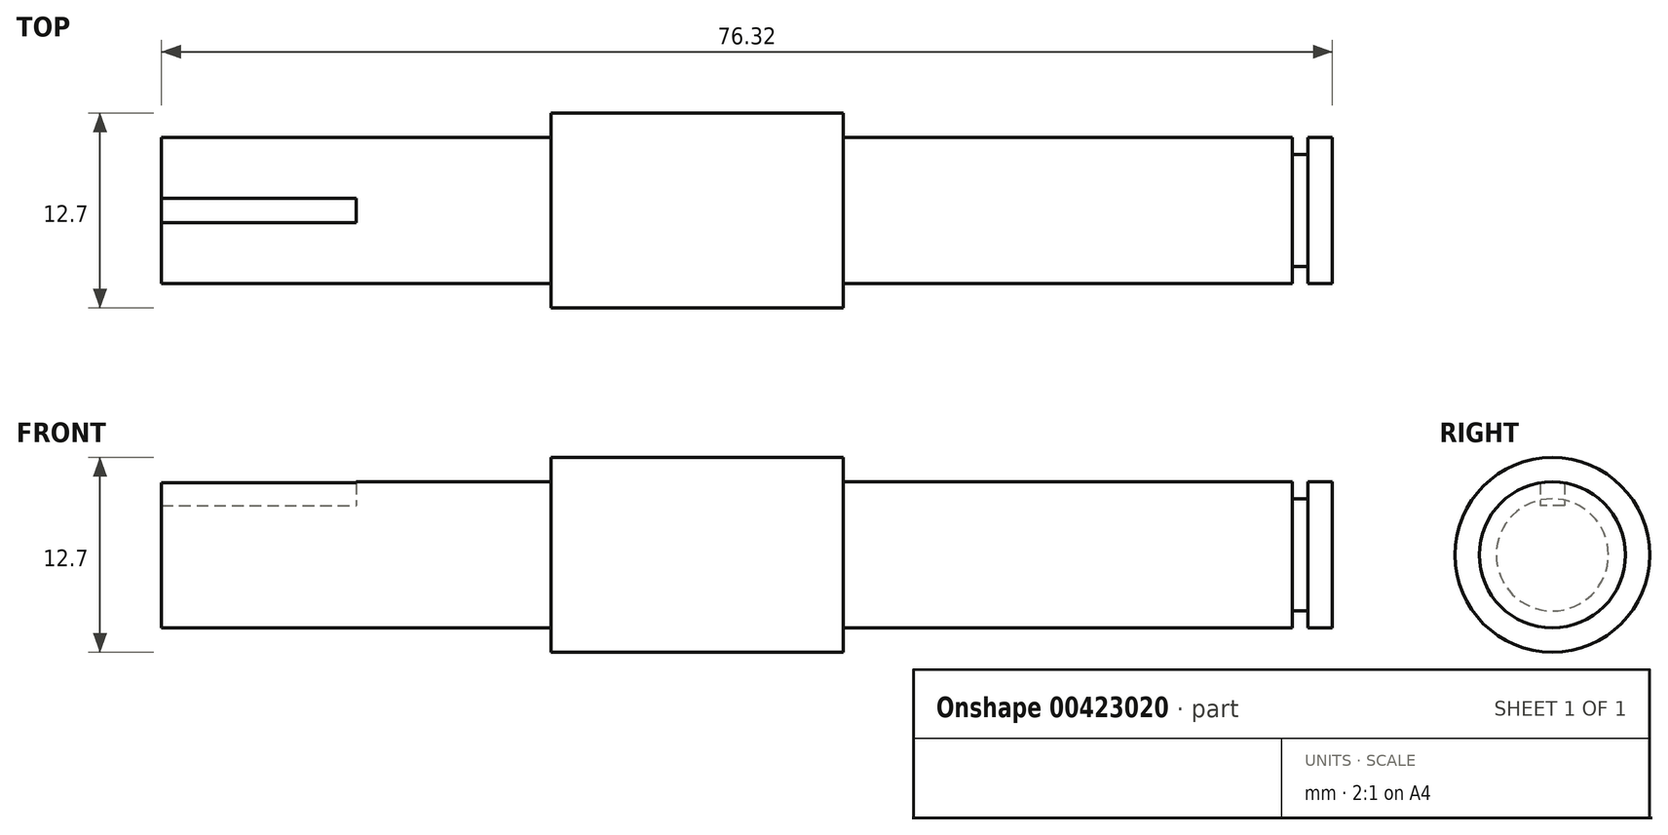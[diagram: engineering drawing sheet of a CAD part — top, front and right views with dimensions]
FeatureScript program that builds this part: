
annotation { "Feature Type Name" : "Feature", "Feature Type Description" : "" }
export const myFeature = defineFeature(function(context is Context, id is Id, definition is map)
    precondition{}
    {
        {
            var Q0;
            Q0=qCreatedBy(makeId("Front.planeOp"),FACE);
            var sketch = newSketch(context, id + "F0", { "sketchPlane" : qUnion([Q0])});
            skLineSegment(sketch, "E0.bottom", {"start": v(3.17, 2.38) * mm, "end": v(-3.18, 2.38) * mm});
            skLineSegment(sketch, "E0.top", {"start": v(3.18, -2.38) * mm, "end": v(-3.17, -2.38) * mm});
            skLineSegment(sketch, "E0.left", {"start": v(3.17, 2.38) * mm, "end": v(3.18, -2.38) * mm});
            skLineSegment(sketch, "E0.right", {"start": v(-3.18, 2.38) * mm, "end": v(-3.17, -2.38) * mm});
            skPoint(sketch, "E0.middle", {"position": v(0, 0) * mm});
            skLineSegment(sketch, "E1.bottom", {"start": v(3.18, -2.38) * mm, "end": v(7.77, -2.38) * mm});
            skLineSegment(sketch, "E1.top", {"start": v(3.17, 2.38) * mm, "end": v(7.77, 2.38) * mm});
            skLineSegment(sketch, "E1.left", {"start": v(3.18, -2.38) * mm, "end": v(3.17, 2.38) * mm});
            skLineSegment(sketch, "E1.right", {"start": v(7.77, -2.38) * mm, "end": v(7.77, 2.38) * mm});
            skLineSegment(sketch, "E2.bottom", {"start": v(-3.17, -2.38) * mm, "end": v(-7.77, -2.38) * mm});
            skLineSegment(sketch, "E2.top", {"start": v(-3.18, 2.38) * mm, "end": v(-7.77, 2.38) * mm});
            skLineSegment(sketch, "E2.left", {"start": v(-3.17, -2.38) * mm, "end": v(-3.18, 2.38) * mm});
            skLineSegment(sketch, "E2.right", {"start": v(-7.77, -2.38) * mm, "end": v(-7.77, 2.38) * mm});
            skPoint(sketch, "E3.oppositeSnap0", {"position": v(0, -2.38) * mm});
            skLineSegment(sketch, "E3.bottom", {"start": v(7.77, 2.38) * mm, "end": v(14.12, 2.38) * mm});
            skLineSegment(sketch, "E3.top", {"start": v(7.77, -2.38) * mm, "end": v(14.12, -2.38) * mm});
            skLineSegment(sketch, "E3.left", {"start": v(7.77, 2.38) * mm, "end": v(7.77, -2.38) * mm});
            skLineSegment(sketch, "E3.right", {"start": v(14.12, 2.38) * mm, "end": v(14.12, -2.38) * mm});
            skLineSegment(sketch, "E4.bottom", {"start": v(-7.77, -2.38) * mm, "end": v(-14.12, -2.38) * mm});
            skLineSegment(sketch, "E4.top", {"start": v(-7.77, 2.38) * mm, "end": v(-14.12, 2.38) * mm});
            skLineSegment(sketch, "E4.right", {"start": v(-14.12, -2.38) * mm, "end": v(-14.12, 2.38) * mm});
            skLineSegment(sketch, "E5.bottom", {"start": v(-14.12, -2.38) * mm, "end": v(-15.14, -2.38) * mm});
            skLineSegment(sketch, "E5.top", {"start": v(-14.12, 2.38) * mm, "end": v(-15.14, 2.38) * mm});
            skLineSegment(sketch, "E5.right", {"start": v(-15.14, -2.38) * mm, "end": v(-15.14, 2.38) * mm});
            skLineSegment(sketch, "E6.bottom", {"start": v(-15.14, -2.38) * mm, "end": v(-34.19, -2.38) * mm});
            skLineSegment(sketch, "E6.top", {"start": v(-15.14, 3.97) * mm, "end": v(-34.19, 3.97) * mm});
            skLineSegment(sketch, "E6.left", {"start": v(-15.14, -2.38) * mm, "end": v(-15.14, 3.97) * mm});
            skLineSegment(sketch, "E6.right", {"start": v(-34.19, -0.8) * mm, "end": v(-34.19, 3.97) * mm});
            skLineSegment(sketch, "E7.bottom", {"start": v(14.12, -2.38) * mm, "end": v(15.14, -2.38) * mm});
            skLineSegment(sketch, "E7.top", {"start": v(14.12, 1.27) * mm, "end": v(15.14, 1.27) * mm});
            skLineSegment(sketch, "E7.left", {"start": v(14.12, -2.38) * mm, "end": v(14.12, 1.27) * mm});
            skLineSegment(sketch, "E7.right", {"start": v(15.14, -2.38) * mm, "end": v(15.14, 1.27) * mm});
            skLineSegment(sketch, "E8.bottom", {"start": v(15.14, -2.38) * mm, "end": v(16.73, -2.38) * mm});
            skLineSegment(sketch, "E8.top", {"start": v(15.14, 2.38) * mm, "end": v(16.73, 2.38) * mm});
            skLineSegment(sketch, "E8.left", {"start": v(15.14, -2.38) * mm, "end": v(15.14, 2.38) * mm});
            skLineSegment(sketch, "E8.right", {"start": v(16.73, -2.38) * mm, "end": v(16.73, 2.38) * mm});
            skLineSegment(sketch, "E9.bottom", {"start": v(-34.19, -2.38) * mm, "end": v(-59.59, -2.38) * mm});
            skLineSegment(sketch, "E9.top", {"start": v(-34.19, 2.38) * mm, "end": v(-59.59, 2.38) * mm});
            skLineSegment(sketch, "E9.left", {"start": v(-34.19, -2.38) * mm, "end": v(-34.19, 2.38) * mm});
            skLineSegment(sketch, "E9.right", {"start": v(-59.59, -2.38) * mm, "end": v(-59.59, 2.38) * mm});
            skSolve(sketch);
        }
        {
            var Q0;
            Q0=qSketchRegion(id+"F0",true);
            var Q1;
            Q1=sQuery(id+"F0.wireOp",EDGE,"E0.top");
            revolve(context, id + "F1", {"entities" : qUnion([Q0]), "axis" : qUnion([Q1]), "revolveType" : RevolveType.FULL});
        }
        {
            var Q0;
            Q0=qCreatedBy(makeId("Front.planeOp"),FACE);
            var sketch = newSketch(context, id + "F2", { "sketchPlane" : qUnion([Q0])});
            skLineSegment(sketch, "E10.bottom", {"start": v(-59.59, 2.42) * mm, "end": v(-46.89, 2.42) * mm});
            skLineSegment(sketch, "E10.top", {"start": v(-59.59, 0.83) * mm, "end": v(-46.89, 0.83) * mm});
            skLineSegment(sketch, "E10.left", {"start": v(-59.59, 2.42) * mm, "end": v(-59.59, 0.83) * mm});
            skLineSegment(sketch, "E10.right", {"start": v(-46.89, 2.42) * mm, "end": v(-46.89, 0.83) * mm});
            skSolve(sketch);
        }
        {
            var Q0;
            Q0 = qSketchRegion(id + "F2", true);
            extrude(context, id + "F3", {"entities" : qUnion([Q0]), "operationType" : NewBodyOperationType.REMOVE, "oppositeDirection" : true, "depth" : 0.8 * mm, "hasSecondDirection" : true, "secondDirectionOppositeDirection" : false, "secondDirectionDepth" : 0.8 * mm});
        }
    });
